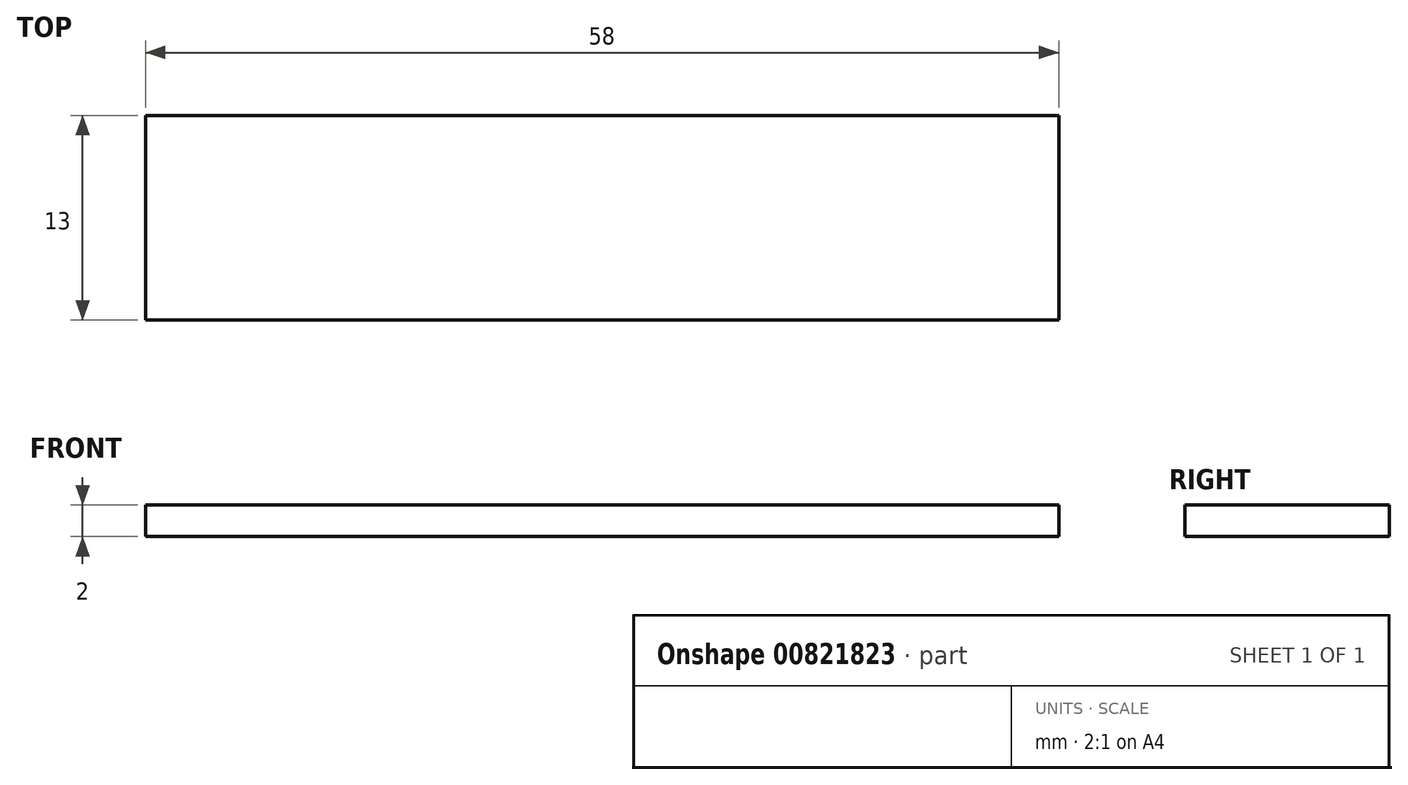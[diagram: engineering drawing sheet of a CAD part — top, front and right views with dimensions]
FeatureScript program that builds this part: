
annotation { "Feature Type Name" : "Feature", "Feature Type Description" : "" }
export const myFeature = defineFeature(function(context is Context, id is Id, definition is map)
    precondition{}
    {
        {
            var Q0;
            Q0=qCreatedBy(makeId("Top.planeOp"),FACE);
            var sketch = newSketch(context, id + "F0", { "sketchPlane" : qUnion([Q0])});
            skLineSegment(sketch, "E0.bottom", {"start": v(29, 6.5) * mm, "end": v(-29, 6.5) * mm});
            skLineSegment(sketch, "E0.top", {"start": v(29, -6.5) * mm, "end": v(-29, -6.5) * mm});
            skLineSegment(sketch, "E0.left", {"start": v(29, 6.5) * mm, "end": v(29, -6.5) * mm});
            skLineSegment(sketch, "E0.right", {"start": v(-29, 6.5) * mm, "end": v(-29, -6.5) * mm});
            skPoint(sketch, "E0.middle", {"position": v(0, 0) * mm});
            skSolve(sketch);
        }
        {
            var Q0;
            Q0 = qSketchRegion(id + "F0", true);
            extrude(context, id + "F1", {"entities" : qUnion([Q0]), "depth" : 2 * mm, "offsetDistance" : 25 * mm});
        }
    });
